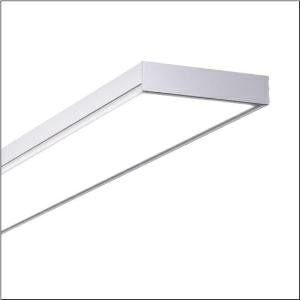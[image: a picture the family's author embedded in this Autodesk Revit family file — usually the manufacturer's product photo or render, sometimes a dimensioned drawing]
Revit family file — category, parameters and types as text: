
# Revit family: apollon_31_surface_51mp26wd2441e
name_source: partatom
category: Lighting Fixtures
units: mm (PartAtom-declared; Revit-internal decimal feet)

## family parameters
Cut with Voids When Loaded = No
Host = Face
Light Source = No
Part Type = Normal
Room Calculation Point = No
Round Connector Dimension = Use Diameter
Shared = No

## types (1)
- Apollon 31 Surface (1 x LED, 4600 lm, 33 W, 4000K)
    Apparent Load = 33 VA
    CIE Flux Codes = 61 87 97 97 100
    Color Rendering = 80
    Color Temperature = 4000K
    Default Elevation = 1800 mm
    Description = Apollon 31 Surface, office luminaire, primary optical cover: micro prismatic cover, of PMMA, light emission: direct distribution, primary light characteristic: symmetric, installation type: surface-mounted, LED, rated luminous flux: 4.600lm, luminous efficacy: 139lm/W, light colour: 840, colour temperature: 4000K, control gear: DALI 2, with terminal, 5-pole, mains connection: 220..240V, AC, 50/60Hz, rated input power: 33W, housing, of sheet steel, coated, metallic grey (RAL 9006), length: 1.545mm, width: 200mm, height: 44mm, protection rating (complete): IP20, protection rating (on room side): IP40, protection rating (lamp compartment, on room side): IP40, insulation class (complete): insulation class I (protective earthing), certification: CE, ENEC, UKCA, impact resistance: IK02, permissible operating ambient temperature: -20..+40°C, standard: EN 60598-2-22, packaging unit: 1 piece
    Height = 44 mm
    Lamp = 1 x LED
    Lamp Light Flux = 4600 lm
    Lamp Power = 33 W
    Lamp count = 1
    Length = 1545 mm
    Luminous efficacy = 139 lm/W
    Manufacturer = Siteco
    ModVariant = No
    Model = 51MP26WD2441E
    Mounting Place = Ceiling
    Mounting Type = Surface mounted
    Number of Poles = 1
    OnlyDefault = Yes
    Power Factor = 1
    Product Name = Apollon 31 Surface
    Product group = office luminaire | ceiling mounted
    ProductGroupID = 301
    Protection Class = Protection class I
    Protection Degree = IP 20
    RLX_Detail_Level = 1
    RLX_Emergency_Light_Flux = 0 lm
    RLX_Emergency_Type = 0
    RLX_Emergency_Type_DB = No
    RlxData = <blob elided: 24153 chars, md5=756cbb6b>
    Socket = socket
    Standby Power = 0 W
    System Light Flux = 4600 lm
    System Power = 33 W
    Type Comments = Product without accessories
    Type Image = l_1313654.jpg
    URL = http://relux.com
    VarID = ---
    Voltage = 0 V
    Weight = 0.00 kg
    Width = 200 mm  [stored 0.656168 ft]

note: [stored X ft] marks values corroborated as IEEE doubles in the binary element streams (Revit-internal decimal feet)

## geometry (parser evidence)
native form markers: Blend x4, Sweep x11
no freeform markers — native parametric forms only
